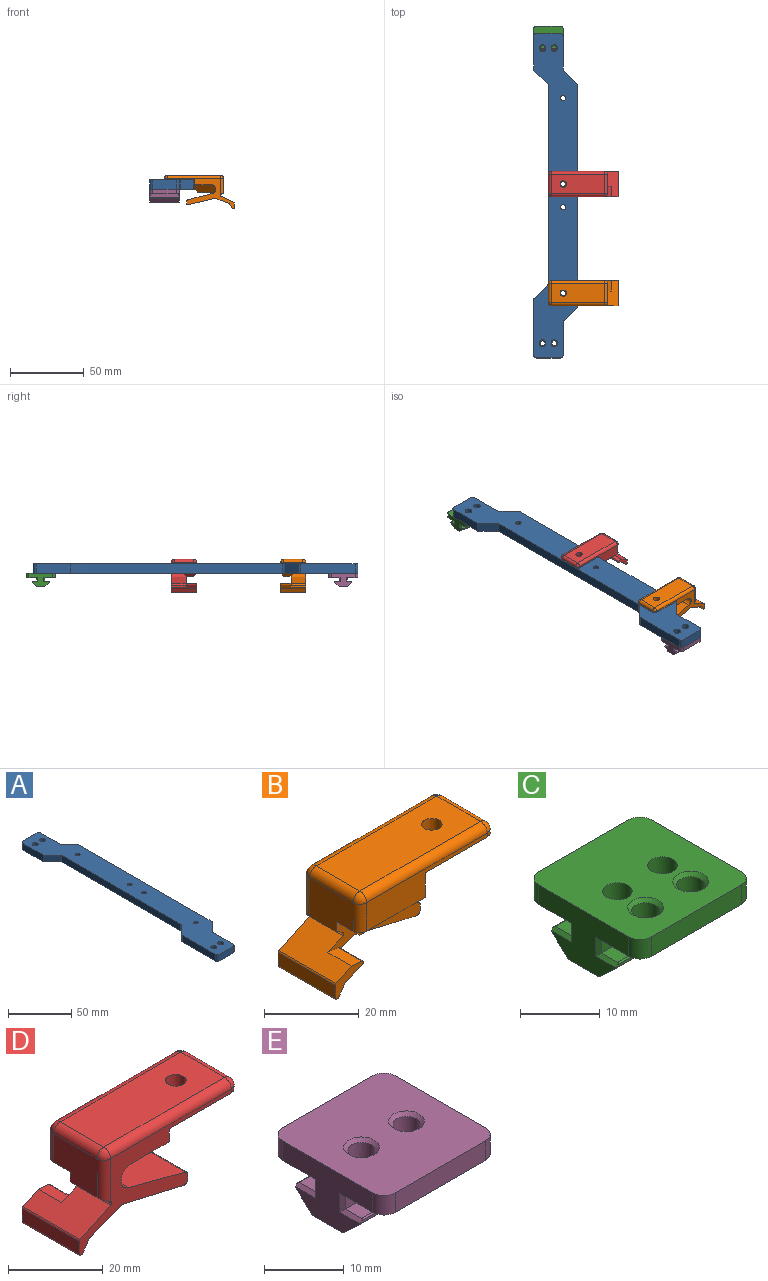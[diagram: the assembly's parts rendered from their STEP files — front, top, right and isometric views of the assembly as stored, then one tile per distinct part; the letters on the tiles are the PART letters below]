
ASSEMBLY  parts=5 mates=4
PART A: 32 faces, bbox 30x220x6.4 mm
  f0: plane 22.9x6.35mm, normal (-1,0,0), area 145.4mm2, adj f8,f9,f20,f31
  f1: plane 16x6.35mm, normal (0,-1,0), area 101.6mm2, adj f8,f9,f16,f17
  f2: plane 22.17x6.35mm, normal (1,0,0), area 140.8mm2, adj f8,f9,f16,f21
  f3: plane 148.34x6.35mm, normal (1,0,0), area 942mm2, adj f8,f9,f13,f14
  f4: plane 22.17x6.35mm, normal (1,0,0), area 140.8mm2, adj f8,f9,f18,f19
  f5: plane 16x6.35mm, normal (0,1,0), area 101.6mm2, adj f8,f9,f19,f20
  f6: plane 134.27x6.35mm, normal (-1,0,0), area 852.6mm2, adj f8,f9,f15,f31
  f7: plane 37.17x6.35mm, normal (-1,0,0), area 236mm2, adj f8,f9,f17,f22
  f8: plane 220x30mm, normal (0,0,1), area 4443.5mm2, adj f0,f1,f2,f3,f4,f5,f6,f7
  f9: plane 220x30mm, normal (0,0,-1), area 4443.5mm2, adj f0,f1,f2,f3,f4,f5,f6,f7
  f10: plane 8.83x8.83mm, normal (-0.71,0.71,0), area 79.3mm2, adj f8,f9,f15,f22
  f11: plane 8.83x8.83mm, normal (0.71,-0.71,0), area 79.3mm2, adj f8,f9,f13,f21
  f12: plane 8.83x8.83mm, normal (0.71,0.71,0), area 79.3mm2, adj f8,f9,f14,f18
  f13: cylinder r=2mm len=6.35mm, axis (0,0,1), area 10mm2, adj f3,f8,f9,f11
  f14: cylinder r=2mm len=6.35mm, axis (0,0,1), area 10mm2, adj f3,f8,f9,f12
  f15: cylinder r=2mm len=6.35mm, axis (0,0,1), area 10mm2, adj f6,f8,f9,f10
  f16: cylinder r=2mm len=6.35mm, axis (0,0,1), area 19.9mm2, adj f1,f2,f8,f9
  f17: cylinder r=2mm len=6.35mm, axis (0,0,-1), area 19.9mm2, adj f1,f7,f8,f9
  f18: cylinder r=2mm len=6.35mm, axis (0,0,1), area 10mm2, adj f4,f8,f9,f12
  f19: cylinder r=2mm len=6.35mm, axis (0,0,-1), area 19.9mm2, adj f4,f5,f8,f9
  f20: cylinder r=2mm len=6.35mm, axis (0,0,1), area 19.9mm2, adj f0,f5,f8,f9
  f21: cylinder r=2mm len=6.35mm, axis (0,0,-1), area 10mm2, adj f2,f8,f9,f11
  f22: cylinder r=2mm len=6.35mm, axis (0,0,1), area 10mm2, adj f7,f8,f9,f10
  f23: cylinder r=2.25mm len=6.35mm, axis (0,0,1), area 89.8mm2, adj f8,f9
  f24: cylinder r=2.25mm len=6.35mm, axis (0,0,1), area 89.8mm2, adj f8,f9
  f25: cylinder r=2.25mm len=6.35mm, axis (0,0,1), area 89.8mm2, adj f8,f9
  f26: cylinder r=2.25mm len=6.35mm, axis (0,0,1), area 89.8mm2, adj f8,f9
  f27: cylinder r=1.75mm len=6.35mm, axis (0,0,1), area 69.8mm2, adj f8,f9
  f28: cylinder r=1.75mm len=6.35mm, axis (0,0,1), area 69.8mm2, adj f8,f9
  f29: cylinder r=1.75mm len=6.35mm, axis (0,0,1), area 69.8mm2, adj f8,f9
  f30: cylinder r=1.75mm len=6.35mm, axis (0,0,1), area 69.8mm2, adj f8,f9
  f31: plane 10x10mm, normal (-0.71,-0.71,0), area 89.8mm2, adj f0,f6,f8,f9
PART B: 50 faces, bbox 47.4x17x22.5 mm
  f0: cylinder r=3mm len=10mm, axis (0,-1,0), area 37mm2, adj f1,f2,f8,f14,f49
  f1: cylinder r=3mm len=7.97mm, axis (0,1,0), area 28.5mm2, adj f0,f9,f14,f49
  f2: plane 27.5x10.44mm, normal (0,-1,0), area 96.4mm2, adj f0,f3,f4,f5,f6,f7,f8,f30
  f3: plane 15.5x5mm, normal (0,0,-1), area 77.5mm2, adj f2,f45,f46,f48,f49
  f4: plane 13x10mm, normal (-1,0,0), area 116.8mm2, adj f2,f5,f16,f20,f43,f45
  f5: plane 10x2.02mm, normal (-0.47,0,-0.88), area 21.9mm2, adj f2,f4,f14,f16,f37
  f6: plane 18.32x10mm, normal (-0.23,0,-0.97), area 188mm2, adj f2,f14,f36,f41
  f7: plane 10x1.26mm, normal (1,0,0), area 12.6mm2, adj f2,f14,f41,f42
  f8: plane 16.82x10mm, normal (0.25,0,0.97), area 173.8mm2, adj f0,f2,f14,f42
  f9: plane 11.31x5mm, normal (0,0,-1), area 56.6mm2, adj f1,f10,f14,f49
  f10: plane 17x6.35mm, normal (1,0,0), area 88.5mm2, adj f9,f11,f14,f15,f46,f49
  f11: plane 20.5x17mm, normal (0,0,-1), area 332.3mm2, adj f10,f12,f14,f15,f18,f25,f26
  f12: plane 13x1mm, normal (1,0,0), area 13mm2, adj f11,f18,f22,f25
  f13: plane 36x13mm, normal (0,0,1), area 453.5mm2, adj f19,f20,f22,f23,f26
  f14: plane 45.37x20.48mm, normal (0,1,0), area 226.8mm2, adj f0,f1,f5,f6,f7,f8,f9,f10
  f15: plane 36x7.35mm, normal (0,-1,0), area 147.1mm2, adj f10,f11,f23,f25,f43,f48
  f16: cylinder r=2mm len=11.07mm, axis (0,0,-1), area 32.6mm2, adj f4,f5,f14,f17
  f17: sphere r=2mm, area 6.3mm2, adj f16,f19,f20
  f18: cylinder r=2mm len=2mm, axis (0,0,1), area 3.1mm2, adj f11,f12,f14,f21
  f19: cylinder r=2mm len=36mm, axis (-1,0,0), area 113.1mm2, adj f13,f14,f17,f21
  f20: cylinder r=2mm len=13mm, axis (0,1,0), area 40.8mm2, adj f4,f13,f17,f44
  f21: sphere r=2mm, area 6.3mm2, adj f18,f19,f22
  f22: cylinder r=2mm len=13mm, axis (0,-1,0), area 40.8mm2, adj f12,f13,f21,f24
  f23: cylinder r=2mm len=36mm, axis (-1,0,0), area 113.1mm2, adj f13,f15,f24,f44
  f24: sphere r=2mm, area 6.3mm2, adj f22,f23,f25
  f25: cylinder r=2mm len=2mm, axis (0,0,1), area 3.1mm2, adj f11,f12,f15,f24
  f26: cylinder r=2.15mm len=4.3mm, axis (0,0,1), area 40.5mm2, adj f11,f13
  f27: plane 17x3.29mm, normal (-1,0,0), area 55.9mm2, adj f14,f32,f33,f38
  f28: plane 17x0.23mm, normal (0,0,-1), area 4mm2, adj f14,f33,f34,f38
  f29: plane 17x2.84mm, normal (0.83,0,-0.56), area 58.4mm2, adj f14,f34,f35,f38
  f30: plane 17x9.08mm, normal (-0.43,0,0.9), area 135.8mm2, adj f2,f14,f32,f37,f38,f39
  f31: plane 17x9.23mm, normal (0.37,0,-0.93), area 135.5mm2, adj f2,f14,f35,f36,f38,f40
  f32: cylinder r=0.5mm len=17mm, axis (0,1,0), area 9.6mm2, adj f14,f27,f30,f38
  f33: cylinder r=0.5mm len=17mm, axis (0,1,0), area 13.4mm2, adj f14,f27,f28,f38
  f34: cylinder r=0.5mm len=17mm, axis (0,1,0), area 8.3mm2, adj f14,f28,f29,f38
  f35: cylinder r=0.5mm len=17mm, axis (0,-1,0), area 5.1mm2, adj f14,f29,f31,f38
  f36: cylinder r=0.5mm len=10mm, axis (0,-1,0), area 3.1mm2, adj f2,f6,f14,f31
  f37: cylinder r=0.5mm len=10mm, axis (0,-1,0), area 11.1mm2, adj f2,f5,f14,f30
  f38: plane 8.39x6.39mm, normal (0,-1,0), area 21.8mm2, adj f27,f28,f29,f30,f31,f32,f33,f34
  f39: plane 7x3.07mm, normal (0.09,0,1), area 21.6mm2, adj f2,f30,f38,f40
  f40: cylinder r=0.5mm len=7mm, axis (0,1,0), area 9.4mm2, adj f2,f31,f38,f39
  f41: cylinder r=1mm len=10mm, axis (0,1,0), area 18mm2, adj f2,f6,f7,f14
  f42: cylinder r=1mm len=10mm, axis (0,1,0), area 13.2mm2, adj f2,f7,f8,f14
  f43: cylinder r=2mm len=7.35mm, axis (0,0,1), area 23.1mm2, adj f4,f15,f44,f47
  f44: sphere r=2mm, area 6.3mm2, adj f20,f23,f43
  f45: plane 5x2mm, normal (-0.71,0,-0.71), area 14.1mm2, adj f2,f3,f4,f47
  f46: plane 9x2mm, normal (0.71,0,-0.71), area 19.8mm2, adj f3,f10,f48,f49
  f47: cone r=2mm half-angle=45deg, axis (0,0,1), area 4.4mm2, adj f43,f45,f48
  f48: plane 17.5x2mm, normal (0,-0.71,-0.71), area 46.7mm2, adj f3,f15,f46,f47
  f49: plane 14.31x5mm, normal (0,0.71,-0.71), area 94.9mm2, adj f0,f1,f3,f9,f10,f46
PART C: 40 faces, bbox 20x20x8.8 mm
  f0: plane 20x7.85mm, normal (0,0,-1), area 126.3mm2, adj f1,f13,f14,f15,f22,f23,f24,f26
  f1: plane 19x2.4mm, normal (0,-1,0), area 45.6mm2, adj f0,f2,f28,f31
  f2: plane 19x2.9mm, normal (0,0,1), area 55.1mm2, adj f1,f16,f35,f36
  f3: plane 20x0.31mm, normal (0,-1,0), area 6.2mm2, adj f14,f15,f16,f17,f35,f36
  f4: plane 20x2.88mm, normal (0,-0.68,-0.73), area 78.8mm2, adj f14,f15,f17,f18
  f5: plane 20x5.34mm, normal (0,0,-1), area 85.3mm2, adj f14,f15,f18,f19,f38,f39
  f6: plane 20x2.88mm, normal (0,0.68,-0.73), area 78.8mm2, adj f14,f15,f19,f20
  f7: plane 20x0.31mm, normal (0,1,0), area 6.2mm2, adj f14,f15,f20,f21,f34,f37
  f8: plane 19x2.9mm, normal (0,0,1), area 55.1mm2, adj f9,f21,f34,f37
  f9: plane 19x2.4mm, normal (0,1,0), area 45.6mm2, adj f8,f10,f29,f30
  f10: plane 20x7.85mm, normal (0,0,-1), area 145.5mm2, adj f9,f11,f14,f15,f25,f27,f29,f30
  f11: plane 16x3mm, normal (0,1,0), area 48mm2, adj f10,f12,f25,f27
  f12: plane 20x20mm, normal (0,0,1), area 343.3mm2, adj f11,f13,f14,f15,f24,f25,f26,f27
  f13: plane 16x3mm, normal (0,-1,0), area 48mm2, adj f0,f12,f24,f26
  f14: plane 16x8.8mm, normal (1,0,0), area 85.4mm2, adj f0,f3,f4,f5,f6,f7,f10,f12
  f15: plane 16x8.8mm, normal (-1,0,0), area 85.4mm2, adj f0,f3,f4,f5,f6,f7,f10,f12
  f16: cylinder r=0.2mm len=19.4mm, axis (-1,0,0), area 6mm2, adj f2,f3,f35,f36
  f17: cylinder r=0.2mm len=20mm, axis (-1,0,0), area 3.3mm2, adj f3,f4,f14,f15
  f18: cylinder r=0.2mm len=20mm, axis (-1,0,0), area 3mm2, adj f4,f5,f14,f15
  f19: cylinder r=0.2mm len=20mm, axis (-1,0,0), area 3mm2, adj f5,f6,f14,f15
  f20: cylinder r=0.2mm len=20mm, axis (-1,0,0), area 3.3mm2, adj f6,f7,f14,f15
  f21: cylinder r=0.2mm len=19.4mm, axis (-1,0,0), area 6mm2, adj f7,f8,f34,f37
  f22: cylinder r=1.75mm len=3.5mm, axis (0,0,1), area 27.5mm2, adj f0,f33
  f23: cylinder r=1.75mm len=3.5mm, axis (0,0,1), area 27.5mm2, adj f0,f32
  f24: cylinder r=2mm len=3mm, axis (0,0,-1), area 9.4mm2, adj f0,f12,f13,f15
  f25: cylinder r=2mm len=3mm, axis (0,0,1), area 9.4mm2, adj f10,f11,f12,f15
  f26: cylinder r=2mm len=3mm, axis (0,0,1), area 9.4mm2, adj f0,f12,f13,f14
  f27: cylinder r=2mm len=3mm, axis (0,0,-1), area 9.4mm2, adj f10,f11,f12,f14
  f28: plane 2.9x0.5mm, normal (-0.71,-0.71,0), area 1.9mm2, adj f0,f1,f15,f35
  f29: plane 2.9x0.5mm, normal (-0.71,0.71,0), area 1.9mm2, adj f9,f10,f15,f34
  f30: plane 2.9x0.5mm, normal (0.71,0.71,0), area 1.9mm2, adj f9,f10,f14,f37
  f31: plane 2.9x0.5mm, normal (0.71,-0.71,0), area 1.9mm2, adj f0,f1,f14,f36
  f32: cone r=1.75mm half-angle=45deg, axis (0,0,1), area 8.9mm2, adj f12,f23
  f33: cone r=1.75mm half-angle=45deg, axis (0,0,1), area 8.9mm2, adj f12,f22
  f34: plane 3.6x0.5mm, normal (-0.71,0,0.71), area 2.4mm2, adj f7,f8,f15,f21,f29
  f35: plane 3.6x0.5mm, normal (-0.71,0,0.71), area 2.4mm2, adj f2,f3,f15,f16,f28
  f36: plane 3.6x0.5mm, normal (0.71,0,0.71), area 2.4mm2, adj f2,f3,f14,f16,f31
  f37: plane 3.6x0.5mm, normal (0.71,0,0.71), area 2.4mm2, adj f7,f8,f14,f21,f30
  f38: cylinder r=1.85mm len=8.8mm, axis (0,0,1), area 102.3mm2, adj f5,f12
  f39: cylinder r=1.85mm len=8.8mm, axis (0,0,1), area 102.3mm2, adj f5,f12
PART D: 50 faces, bbox 47.4x17x22.5 mm
  f0: cylinder r=3mm len=7.97mm, axis (0,-1,0), area 28.5mm2, adj f1,f9,f14,f49
  f1: cylinder r=3mm len=10mm, axis (0,1,0), area 37mm2, adj f0,f2,f8,f14,f49
  f2: plane 27.5x10.44mm, normal (0,1,0), area 96.4mm2, adj f1,f3,f4,f5,f6,f7,f8,f30
  f3: plane 15.5x5mm, normal (0,0,-1), area 77.5mm2, adj f2,f45,f46,f48,f49
  f4: plane 13x10mm, normal (-1,0,0), area 116.7mm2, adj f2,f5,f16,f20,f43,f45
  f5: plane 10x2.02mm, normal (-0.47,0,-0.88), area 21.9mm2, adj f2,f4,f14,f16,f37
  f6: plane 18.32x10mm, normal (-0.23,0,-0.97), area 188mm2, adj f2,f14,f36,f41
  f7: plane 10x1.26mm, normal (1,0,0), area 12.6mm2, adj f2,f14,f41,f42
  f8: plane 16.82x10mm, normal (0.25,0,0.97), area 173.8mm2, adj f1,f2,f14,f42
  f9: plane 11.31x5mm, normal (0,0,-1), area 56.6mm2, adj f0,f10,f14,f49
  f10: plane 17x6.35mm, normal (1,0,0), area 88.4mm2, adj f9,f11,f14,f15,f46,f49
  f11: plane 20.5x17mm, normal (0,0,-1), area 332.3mm2, adj f10,f12,f14,f15,f18,f25,f26
  f12: plane 13x1mm, normal (1,0,0), area 13mm2, adj f11,f18,f22,f25
  f13: plane 36x13mm, normal (0,0,1), area 453.5mm2, adj f19,f20,f22,f23,f26
  f14: plane 45.37x20.48mm, normal (0,-1,0), area 226.8mm2, adj f0,f1,f5,f6,f7,f8,f9,f10
  f15: plane 36x7.35mm, normal (0,1,0), area 147.1mm2, adj f10,f11,f23,f25,f43,f48
  f16: cylinder r=2mm len=11.07mm, axis (0,0,-1), area 32.6mm2, adj f4,f5,f14,f17
  f17: sphere r=2mm, area 6.3mm2, adj f16,f19,f20
  f18: cylinder r=2mm len=2mm, axis (0,0,1), area 3.1mm2, adj f11,f12,f14,f21
  f19: cylinder r=2mm len=36mm, axis (-1,0,0), area 113.1mm2, adj f13,f14,f17,f21
  f20: cylinder r=2mm len=13mm, axis (0,-1,0), area 40.8mm2, adj f4,f13,f17,f44
  f21: sphere r=2mm, area 6.3mm2, adj f18,f19,f22
  f22: cylinder r=2mm len=13mm, axis (0,1,0), area 40.8mm2, adj f12,f13,f21,f24
  f23: cylinder r=2mm len=36mm, axis (-1,0,0), area 113.1mm2, adj f13,f15,f24,f44
  f24: sphere r=2mm, area 6.3mm2, adj f22,f23,f25
  f25: cylinder r=2mm len=2mm, axis (0,0,1), area 3.1mm2, adj f11,f12,f15,f24
  f26: cylinder r=2.15mm len=4.3mm, axis (0,0,1), area 40.5mm2, adj f11,f13
  f27: plane 17x3.29mm, normal (-1,0,0), area 55.9mm2, adj f14,f32,f33,f38
  f28: plane 17x0.23mm, normal (0,0,-1), area 4mm2, adj f14,f33,f34,f38
  f29: plane 17x2.84mm, normal (0.83,0,-0.56), area 58.4mm2, adj f14,f34,f35,f38
  f30: plane 17x9.08mm, normal (-0.43,0,0.9), area 135.8mm2, adj f2,f14,f32,f37,f38,f39
  f31: plane 17x9.23mm, normal (0.37,0,-0.93), area 135.5mm2, adj f2,f14,f35,f36,f38,f40
  f32: cylinder r=0.5mm len=17mm, axis (0,-1,0), area 9.6mm2, adj f14,f27,f30,f38
  f33: cylinder r=0.5mm len=17mm, axis (0,-1,0), area 13.4mm2, adj f14,f27,f28,f38
  f34: cylinder r=0.5mm len=17mm, axis (0,-1,0), area 8.3mm2, adj f14,f28,f29,f38
  f35: cylinder r=0.5mm len=17mm, axis (0,1,0), area 5.1mm2, adj f14,f29,f31,f38
  f36: cylinder r=0.5mm len=10mm, axis (0,1,0), area 3.1mm2, adj f2,f6,f14,f31
  f37: cylinder r=0.5mm len=10mm, axis (0,1,0), area 11.1mm2, adj f2,f5,f14,f30
  f38: plane 8.39x6.39mm, normal (0,1,0), area 21.8mm2, adj f27,f28,f29,f30,f31,f32,f33,f34
  f39: plane 7x3.07mm, normal (0.09,0,1), area 21.6mm2, adj f2,f30,f38,f40
  f40: cylinder r=0.5mm len=7mm, axis (0,-1,0), area 9.4mm2, adj f2,f31,f38,f39
  f41: cylinder r=1mm len=10mm, axis (0,-1,0), area 18mm2, adj f2,f6,f7,f14
  f42: cylinder r=1mm len=10mm, axis (0,-1,0), area 13.2mm2, adj f2,f7,f8,f14
  f43: cylinder r=2mm len=7.35mm, axis (0,0,-1), area 23.1mm2, adj f4,f15,f44,f47
  f44: sphere r=2mm, area 6.3mm2, adj f20,f23,f43
  f45: plane 5x2mm, normal (-0.71,0,-0.71), area 14.1mm2, adj f2,f3,f4,f47
  f46: plane 9x2mm, normal (0.71,0,-0.71), area 19.8mm2, adj f3,f10,f48,f49
  f47: cone r=2mm half-angle=45deg, axis (0,0,1), area 4.4mm2, adj f43,f45,f48
  f48: plane 17.5x2mm, normal (0,0.71,-0.71), area 46.7mm2, adj f3,f15,f46,f47
  f49: plane 14.31x5mm, normal (0,-0.71,-0.71), area 94.9mm2, adj f0,f1,f3,f9,f10,f46
PART E: 38 faces, bbox 20x20x8.8 mm
  f0: plane 20x7.85mm, normal (0,0,-1), area 145.5mm2, adj f1,f13,f14,f15,f24,f26,f28,f31
  f1: plane 19x2.4mm, normal (0,-1,0), area 45.6mm2, adj f0,f2,f28,f31
  f2: plane 19x2.9mm, normal (0,0,1), area 55.1mm2, adj f1,f16,f35,f36
  f3: plane 20x0.31mm, normal (0,-1,0), area 6.2mm2, adj f14,f15,f16,f17,f35,f36
  f4: plane 20x2.88mm, normal (0,-0.68,-0.73), area 78.8mm2, adj f14,f15,f17,f18
  f5: plane 20x5.34mm, normal (0,0,-1), area 87.6mm2, adj f14,f15,f18,f19,f22,f23
  f6: plane 20x2.88mm, normal (0,0.68,-0.73), area 78.8mm2, adj f14,f15,f19,f20
  f7: plane 20x0.31mm, normal (0,1,0), area 6.2mm2, adj f14,f15,f20,f21,f34,f37
  f8: plane 19x2.9mm, normal (0,0,1), area 55.1mm2, adj f9,f21,f34,f37
  f9: plane 19x2.4mm, normal (0,1,0), area 45.6mm2, adj f8,f10,f29,f30
  f10: plane 20x7.85mm, normal (0,0,-1), area 145.5mm2, adj f9,f11,f14,f15,f25,f27,f29,f30
  f11: plane 16x3mm, normal (0,1,0), area 48mm2, adj f10,f12,f25,f27
  f12: plane 20x20mm, normal (0,0,1), area 364.8mm2, adj f11,f13,f14,f15,f24,f25,f26,f27
  f13: plane 16x3mm, normal (0,-1,0), area 48mm2, adj f0,f12,f24,f26
  f14: plane 16x8.8mm, normal (1,0,0), area 85.4mm2, adj f0,f3,f4,f5,f6,f7,f10,f12
  f15: plane 16x8.8mm, normal (-1,0,0), area 85.4mm2, adj f0,f3,f4,f5,f6,f7,f10,f12
  f16: cylinder r=0.2mm len=19.4mm, axis (-1,0,0), area 6mm2, adj f2,f3,f35,f36
  f17: cylinder r=0.2mm len=20mm, axis (-1,0,0), area 3.3mm2, adj f3,f4,f14,f15
  f18: cylinder r=0.2mm len=20mm, axis (-1,0,0), area 3mm2, adj f4,f5,f14,f15
  f19: cylinder r=0.2mm len=20mm, axis (-1,0,0), area 3mm2, adj f5,f6,f14,f15
  f20: cylinder r=0.2mm len=20mm, axis (-1,0,0), area 3.3mm2, adj f6,f7,f14,f15
  f21: cylinder r=0.2mm len=19.4mm, axis (-1,0,0), area 6mm2, adj f7,f8,f34,f37
  f22: cylinder r=1.75mm len=8.3mm, axis (0,0,1), area 91.3mm2, adj f5,f33
  f23: cylinder r=1.75mm len=8.3mm, axis (0,0,1), area 91.3mm2, adj f5,f32
  f24: cylinder r=2mm len=3mm, axis (0,0,-1), area 9.4mm2, adj f0,f12,f13,f15
  f25: cylinder r=2mm len=3mm, axis (0,0,1), area 9.4mm2, adj f10,f11,f12,f15
  f26: cylinder r=2mm len=3mm, axis (0,0,1), area 9.4mm2, adj f0,f12,f13,f14
  f27: cylinder r=2mm len=3mm, axis (0,0,-1), area 9.4mm2, adj f10,f11,f12,f14
  f28: plane 2.9x0.5mm, normal (-0.71,-0.71,0), area 1.9mm2, adj f0,f1,f15,f35
  f29: plane 2.9x0.5mm, normal (-0.71,0.71,0), area 1.9mm2, adj f9,f10,f15,f34
  f30: plane 2.9x0.5mm, normal (0.71,0.71,0), area 1.9mm2, adj f9,f10,f14,f37
  f31: plane 2.9x0.5mm, normal (0.71,-0.71,0), area 1.9mm2, adj f0,f1,f14,f36
  f32: cone r=1.75mm half-angle=45deg, axis (0,0,1), area 8.9mm2, adj f12,f23
  f33: cone r=1.75mm half-angle=45deg, axis (0,0,1), area 8.9mm2, adj f12,f22
  f34: plane 3.6x0.5mm, normal (-0.71,0,0.71), area 2.4mm2, adj f7,f8,f15,f21,f29
  f35: plane 3.6x0.5mm, normal (-0.71,0,0.71), area 2.4mm2, adj f2,f3,f15,f16,f28
  f36: plane 3.6x0.5mm, normal (0.71,0,0.71), area 2.4mm2, adj f2,f3,f14,f16,f31
  f37: plane 3.6x0.5mm, normal (0.71,0,0.71), area 2.4mm2, adj f7,f8,f14,f21,f30
PLACE A t=(3.46,-65.07,32.74)mm fixed
PLACE B rot(axis=(0,0,-1),180deg) t=(43.46,134.93,32.74)mm
PLACE C t=(3.46,139.93,32.74)mm
PLACE D rot(axis=(0,0,1),180deg) t=(43.46,134.93,32.74)mm
PLACE E t=(3.46,-65.07,32.74)mm
MATE fastened A.f23 <-> C.f32  axis (0,0,-1) through (17.46,134.93,34.24)mm
MATE fastened A.f25 <-> E.f32  axis (0,0,-1) through (17.46,-65.07,34.24)mm
MATE fastened D.f26 <-> A.f29  axis (0,0,-1) through (23.46,42.83,40.59)mm
MATE fastened B.f26 <-> A.f30  axis (0,0,-1) through (23.46,-31.17,40.59)mm
